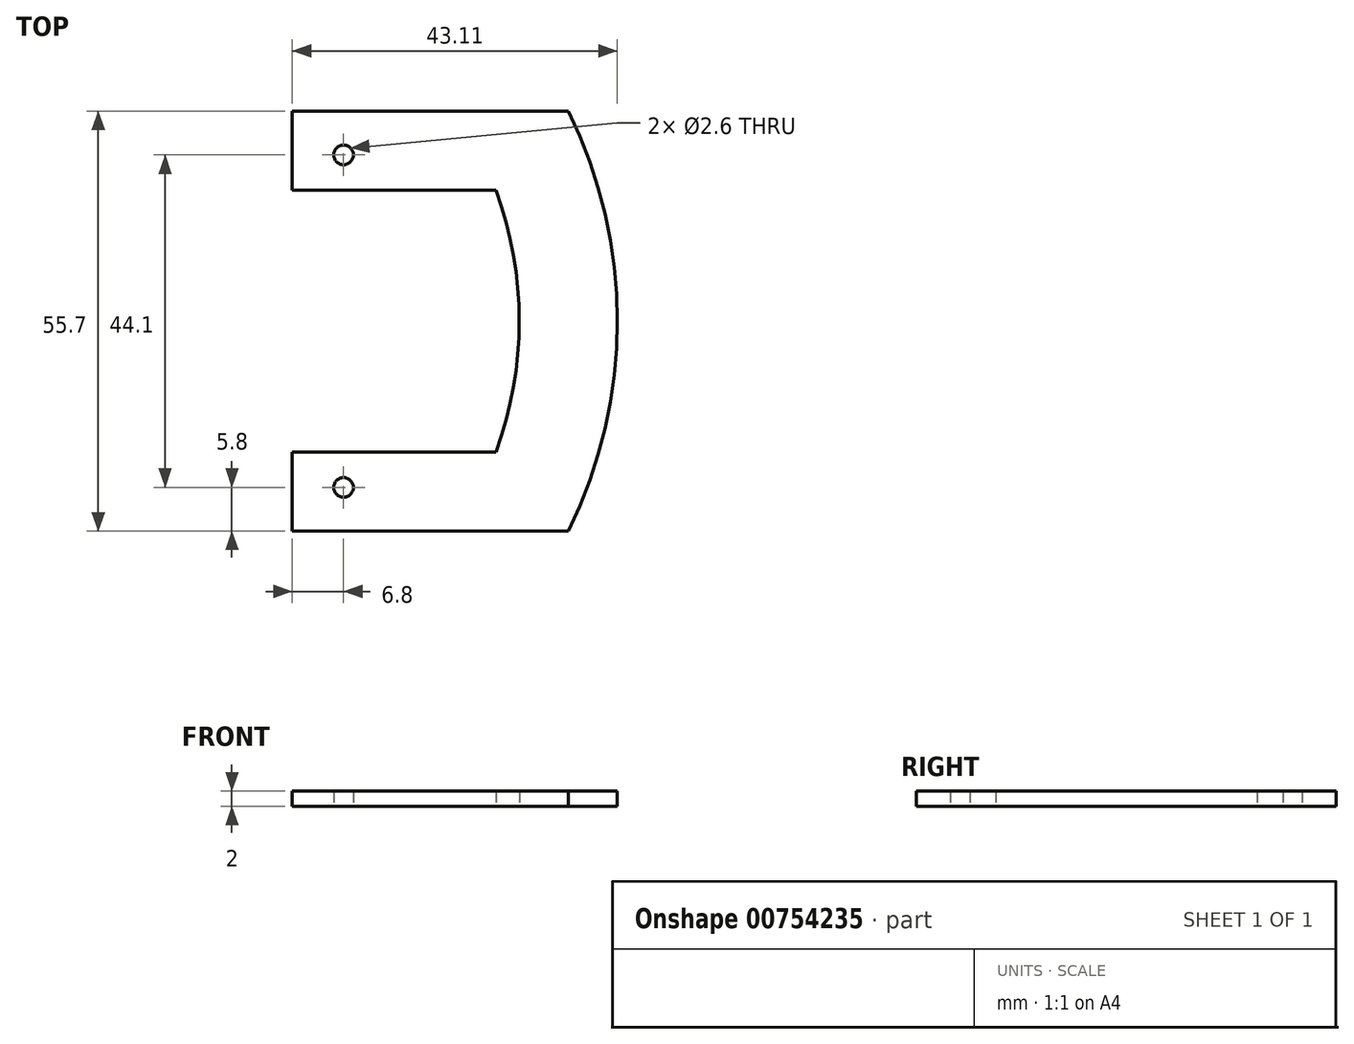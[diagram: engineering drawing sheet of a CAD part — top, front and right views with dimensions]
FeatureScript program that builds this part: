
annotation { "Feature Type Name" : "Feature", "Feature Type Description" : "" }
export const myFeature = defineFeature(function(context is Context, id is Id, definition is map)
    precondition{}
    {
        {
            var Q0;
            Q0=qCreatedBy(makeId("Top.planeOp"),FACE);
            var sketch = newSketch(context, id + "F0", { "sketchPlane" : qUnion([Q0])});
            skLineSegment(sketch, "E0", {"start": v(0, 0) * mm, "end": v(0, 44.1) * mm, "construction": true});
            skCircle(sketch, "E1", {"center": v(0, 0) * mm, "radius": 1.3 * mm});
            skCircle(sketch, "E2", {"center": v(0, 44.1) * mm, "radius": 1.3 * mm});
            skLineSegment(sketch, "E3", {"start": v(-6.8, 4.7) * mm, "end": v(-6.8, -5.8) * mm});
            skLineSegment(sketch, "E4", {"start": v(-6.8, -5.8) * mm, "end": v(29.82, -5.8) * mm});
            skLineSegment(sketch, "E5", {"start": v(-6.8, 4.7) * mm, "end": v(20.2, 4.7) * mm});
            skLineSegment(sketch, "E6", {"start": v(0, 22.05) * mm, "end": v(23.3, 22.05) * mm, "construction": true});
            skLineSegment(sketch, "E7.MirrorCS", {"start": v(-6.8, 39.4) * mm, "end": v(-6.8, 49.9) * mm});
            skLineSegment(sketch, "E8.MirrorCS", {"start": v(-6.8, 49.9) * mm, "end": v(29.82, 49.9) * mm});
            skLineSegment(sketch, "E9.MirrorCS", {"start": v(-6.8, 39.4) * mm, "end": v(20.2, 39.4) * mm});
            skArc(sketch, "E10", {"start": v(20.2, 4.7) * mm, "mid": v(23.3, 22.05) * mm, "end": v(20.2, 39.4) * mm});
            skArc(sketch, "E11", {"start": v(29.82, -5.8) * mm, "mid": v(36.3, 22.05) * mm, "end": v(29.82, 49.9) * mm});
            skSolve(sketch);
        }
        {
            var Q0;
            Q0 = qSketchRegion(id + "F0", true);
            extrude(context, id + "F1", {"entities" : qUnion([Q0]), "depth" : 2 * mm, "offsetDistance" : 25 * mm});
        }
    });
